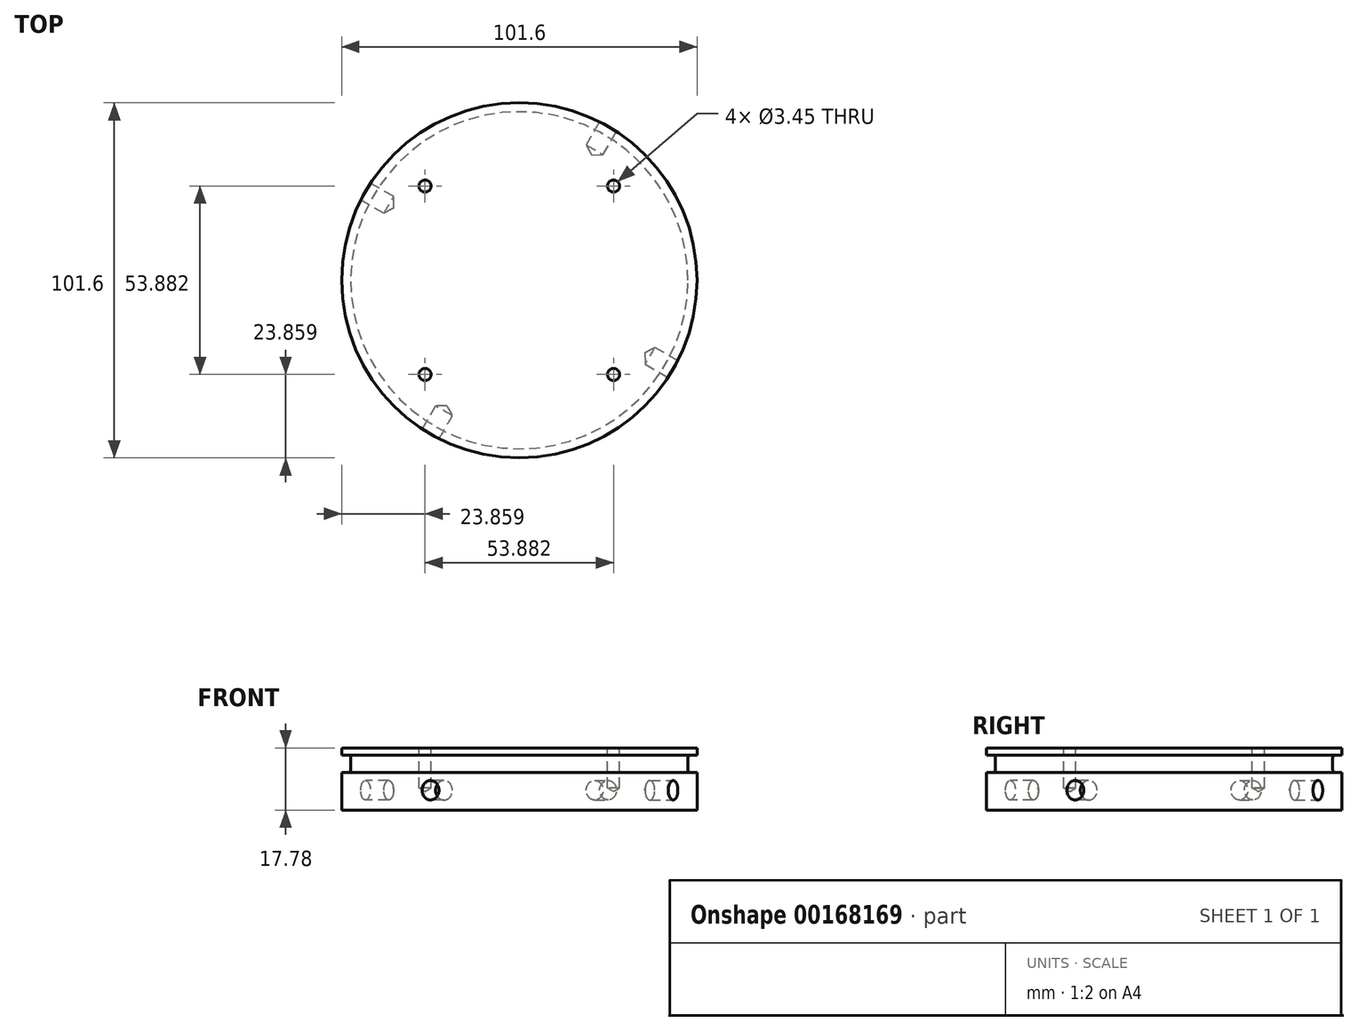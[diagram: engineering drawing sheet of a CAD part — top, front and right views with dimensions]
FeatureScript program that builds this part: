
annotation { "Feature Type Name" : "Feature", "Feature Type Description" : "" }
export const myFeature = defineFeature(function(context is Context, id is Id, definition is map)
    precondition{}
    {
        {
            var Q0;
            Q0=qCreatedBy(makeId("Top.planeOp"),FACE);
            var sketch = newSketch(context, id + "F0", { "sketchPlane" : qUnion([Q0])});
            skCircle(sketch, "E0", {"center": v(0, 0) * mm, "radius": 50.8 * mm});
            skSolve(sketch);
        }
        {
            var Q0;
            Q0=makeQuery(id+"F0.imprint","IMPRINT",FACE,{"disambiguationData":[TD([[makeQuery(id+"F0.imprint","IMPRINT",EDGE,{"derivedFrom":sQuery(id+"F0.wireOp",EDGE,"E0")}),1.0]])]});
            extrude(context, id + "F1", {"entities" : qUnion([Q0]), "depth" : 17.78 * mm});
        }
        {
            var Q0;
            {var subQ0=makeQuery(id+"FhJubWmbG7UBd7M_1.boolean.opBoolean","COPY",FACE,{"derivedFrom":makeQuery(id+"FhJubWmbG7UBd7M_1.opExtrude","SWEPT_FACE",FACE,{"disambiguationData":[OSD([sQuery(id+"FRuIeaWD6VeLny9_1.wireOp",EDGE,"idePJaX5-tPPE-BKw2-N1m4-zZUQrY6AHjir")])]})});Q0=makeQuery(id+"FOQC5dfjhO448EJ_1.boolean.opBoolean","SPLIT",FACE,{"disambiguationData":[TD([subQ0])],"derivedFrom":makeQuery(id+"FkcieFRIapZdHPD_1.boolean.opBoolean","SPLIT",FACE,{"disambiguationData":[TD([subQ0])],"derivedFrom":makeQuery(id+"F1.opExtrude","CAP_FACE",FACE,{"disambiguationData":[OSD([sQuery(id+"F0.wireOp",EDGE,"E0")])],"isStart":false})})});}
            var sketch = newSketch(context, id + "F2", { "sketchPlane" : qUnion([Q0])});
            skCircle(sketch, "E1", {"center": v(0, 0) * mm, "radius": 38.1 * mm, "construction": true});
            skLineSegment(sketch, "E2", {"start": v(0, 0) * mm, "end": v(38.1, 0) * mm, "construction": true});
            skPoint(sketch, "E3", {"position": v(38.1, 0) * mm});
            skLineSegment(sketch, "E4", {"start": v(0, 0) * mm, "end": v(26.94, -26.94) * mm, "construction": true});
            skPoint(sketch, "E5", {"position": v(26.94, -26.94) * mm});
            skPoint(sketch, "E6.1.0", {"position": v(26.94, 26.94) * mm});
            skPoint(sketch, "E6.2.0", {"position": v(-26.94, 26.94) * mm});
            skPoint(sketch, "E6.3.0", {"position": v(-26.94, -26.94) * mm});
            skSolve(sketch);
        }
        {
            var Q0;
            Q0=sQuery(id+"F2.wireOp",VERTEX,"E5");
            var Q1;
            Q1=sQuery(id+"F2.wireOp",VERTEX,"E6.3.0");
            var Q2;
            Q2=sQuery(id+"F2.wireOp",VERTEX,"E6.2.0");
            var Q3;
            Q3=sQuery(id+"F2.wireOp",VERTEX,"E6.1.0");
            var Q4;
            Q4=makeQuery(id+"F1.opExtrude","SWEPT_BODY",BODY,{"disambiguationData":[OSD([sQuery(id+"F0.wireOp",EDGE,"E0")])]});
            hole(context, id + "F3", {"style" : HoleStyle.SIMPLE, "endStyle" : HoleEndStyle.BLIND, "standardTappedOrClearance" : lookupTablePath({ "standard" : "ANSI", "engagement" : "75%", "pitch" : "32 tpi", "size" : "#8", "type" : "Tapped" }), "standardBlindInLast" : lookupTablePath({ "standard" : "ANSI", "engagement" : "75%", "pitch" : "32 tpi", "size" : "#8", "type" : "Tapped" }), "holeDiameter" : 3.45 * mm, "holeDepth" : 11.43 * mm, "locations" : qUnion([Q0, Q1, Q2, Q3]), "scope" : qUnion([Q4]), "majorDiameter" : 4.17 * mm});
        }
        {
            var Q0;
            Q0=makeQuery(id+"FOQC5dfjhO448EJ_1.boolean.opBoolean","SPLIT",FACE,{"disambiguationData":[TD([makeQuery(id+"FhJubWmbG7UBd7M_1.boolean.opBoolean","COPY",FACE,{"derivedFrom":makeQuery(id+"FhJubWmbG7UBd7M_1.opExtrude","SWEPT_FACE",FACE,{"disambiguationData":[OSD([sQuery(id+"FRuIeaWD6VeLny9_1.wireOp",EDGE,"idePJaX5-tPPE-BKw2-N1m4-zZUQrY6AHjir")])]})})])],"derivedFrom":makeQuery(id+"F1.opExtrude","CAP_FACE",FACE,{"disambiguationData":[OSD([sQuery(id+"F0.wireOp",EDGE,"E0")])],"isStart":false})});
            cPlane(context, id + "F4", {"entities" : qUnion([Q0]), "cplaneType" : CPlaneType.OFFSET, "offset" : 2.03 * mm, "oppositeDirection" : true, "width" : 152.4 * mm, "height" : 152.4 * mm});
        }
        {
            var Q0;
            Q0=qCreatedBy(id+"F4.planeOp",FACE);
            var sketch = newSketch(context, id + "F5", { "sketchPlane" : qUnion([Q0])});
            skCircle(sketch, "E7", {"center": v(0, 0) * mm, "radius": 48.2 * mm});
            skCircle(sketch, "E8.0", {"center": v(0, 0) * mm, "radius": 50.8 * mm});
            skSolve(sketch);
        }
        {
            var Q0;
            Q0=qSketchRegion(id+"F5",true);
            extrude(context, id + "F6", {"entities" : qUnion([Q0]), "operationType" : NewBodyOperationType.REMOVE, "oppositeDirection" : true, "depth" : 5 * mm});
        }
        {
            var Q0;
            Q0=makeQuery(id+"F6.boolean.opBoolean","COPY",EDGE,{"derivedFrom":makeQuery(id+"F6.opExtrude","CAP_EDGE",EDGE,{"disambiguationData":[OSD([sQuery(id+"F5.wireOp",EDGE,"E7")])],"isStart":false})});
            var Q1;
            Q1=makeQuery(id+"F6.boolean.opBoolean","COPY",EDGE,{"derivedFrom":makeQuery(id+"F6.opExtrude","CAP_EDGE",EDGE,{"disambiguationData":[OSD([sQuery(id+"F5.wireOp",EDGE,"E7")])],"isStart":true})});
            fillet(context, id + "F7", {"entities" : qUnion([Q0, Q1]), "radius" : 0.76 * mm, "tangentPropagation" : true, "allowEdgeOverflow" : false});
        }
        {
            var Q0;
            {var subQ1=sQuery(id+"F0.wireOp",EDGE,"E0");var subQ2=makeQuery(id+"F1.opExtrude","SWEPT_FACE",FACE,{"disambiguationData":[OSD([subQ1])]});Q0=makeQuery(id+"FkcieFRIapZdHPD_1.boolean.opBoolean","SPLIT",FACE,{"disambiguationData":[TD([subQ2])],"derivedFrom":makeQuery(id+"F1.opExtrude","CAP_FACE",FACE,{"disambiguationData":[OSD([subQ1])],"isStart":false})});}
            var sketch = newSketch(context, id + "F8", { "sketchPlane" : qUnion([Q0])});
            skCircle(sketch, "E9.0", {"center": v(0, 0) * mm, "radius": 50.8 * mm, "construction": true});
            skPoint(sketch, "E10", {"position": v(-25.4, -44) * mm});
            skLineSegment(sketch, "E11", {"start": v(0, -50.8) * mm, "end": v(0, 0) * mm, "construction": true});
            skLineSegment(sketch, "E12", {"start": v(0, 0) * mm, "end": v(-17.96, -31.1) * mm, "construction": true});
            skLineSegment(sketch, "E13", {"start": v(-17.96, -31.1) * mm, "end": v(-25.4, -44) * mm, "construction": true});
            skLineSegment(sketch, "E14", {"start": v(0, 0) * mm, "end": v(25.4, 44) * mm, "construction": true});
            skLineSegment(sketch, "E15", {"start": v(25.4, 44) * mm, "end": v(0, 0) * mm, "construction": true});
            skLineSegment(sketch, "E16", {"start": v(44, -25.4) * mm, "end": v(0, 0) * mm, "construction": true});
            skLineSegment(sketch, "E17", {"start": v(0, 0) * mm, "end": v(-44, 25.4) * mm, "construction": true});
            skPoint(sketch, "E18", {"position": v(25.4, 44) * mm});
            skPoint(sketch, "E19", {"position": v(44, -25.4) * mm});
            skPoint(sketch, "E20", {"position": v(-44, 25.4) * mm});
            skSolve(sketch);
        }
        {
            var Q0;
            Q0=qCreatedBy(makeId("Front.planeOp"),FACE);
            var sketch = newSketch(context, id + "F9", { "sketchPlane" : qUnion([Q0])});
            skLineSegment(sketch, "E21", {"start": v(0, 0) * mm, "end": v(0, 38.57) * mm, "construction": true});
            skSolve(sketch);
        }
        {
            var Q0;
            Q0=sQuery(id+"F9.wireOp",EDGE,"E21");
            cPlane(context, id + "F10", {"entities" : qUnion([Q0]), "cplaneType" : CPlaneType.LINE_ANGLE, "offset" : 25.4 * mm, "angle" : 60 * degree, "width" : 152.4 * mm, "height" : 152.4 * mm});
        }
        {
            var Q0;
            Q0=sQuery(id+"F8.wireOp",VERTEX,"E10");
            var Q1;
            Q1=qCreatedBy(id+"F10.planeOp",FACE);
            cPlane(context, id + "F11", {"entities" : qUnion([Q0, Q1]), "cplaneType" : CPlaneType.PLANE_POINT, "offset" : 25.4 * mm, "width" : 152.4 * mm, "height" : 152.4 * mm});
        }
        {
            var Q0;
            Q0=qCreatedBy(id+"F11.planeOp",FACE);
            var Q1;
            Q1=sQuery(id+"F8.wireOp",VERTEX,"E18");
            cPlane(context, id + "F12", {"entities" : qUnion([Q0, Q1]), "cplaneType" : CPlaneType.PLANE_POINT, "offset" : 25.4 * mm, "width" : 152.4 * mm, "height" : 152.4 * mm});
        }
        {
            var Q0;
            Q0=sQuery(id+"F9.wireOp",EDGE,"E21");
            cPlane(context, id + "F13", {"entities" : qUnion([Q0]), "cplaneType" : CPlaneType.LINE_ANGLE, "offset" : 25.4 * mm, "angle" : 150 * degree, "width" : 152.4 * mm, "height" : 152.4 * mm});
        }
        {
            var Q0;
            Q0=sQuery(id+"F8.wireOp",VERTEX,"E20");
            var Q1;
            Q1=qCreatedBy(id+"F13.planeOp",FACE);
            cPlane(context, id + "F14", {"entities" : qUnion([Q0, Q1]), "cplaneType" : CPlaneType.PLANE_POINT, "offset" : 25.4 * mm, "width" : 152.4 * mm, "height" : 152.4 * mm});
        }
        {
            var Q0;
            Q0=qCreatedBy(id+"F13.planeOp",FACE);
            var Q1;
            Q1=sQuery(id+"F8.wireOp",VERTEX,"E19");
            cPlane(context, id + "F15", {"entities" : qUnion([Q0, Q1]), "cplaneType" : CPlaneType.PLANE_POINT, "offset" : 25.4 * mm, "width" : 152.4 * mm, "height" : 152.4 * mm});
        }
        {
            var Q0;
            Q0=qCreatedBy(id+"F11.planeOp",FACE);
            var sketch = newSketch(context, id + "F16", { "sketchPlane" : qUnion([Q0])});
            skLineSegment(sketch, "E22", {"start": v(0, 0) * mm, "end": v(0, 5.66) * mm, "construction": true});
            skPoint(sketch, "E23", {"position": v(0, 5.66) * mm});
            skSolve(sketch);
        }
        {
            var Q0;
            Q0=qCreatedBy(id+"F12.planeOp",FACE);
            var sketch = newSketch(context, id + "F17", { "sketchPlane" : qUnion([Q0])});
            skPoint(sketch, "E24", {"position": v(0, 5.66) * mm});
            skLineSegment(sketch, "E25.0", {"start": v(0, 0) * mm, "end": v(0, 5.66) * mm, "construction": true});
            skSolve(sketch);
        }
        {
            var Q0;
            Q0=qCreatedBy(id+"F14.planeOp",FACE);
            var sketch = newSketch(context, id + "F18", { "sketchPlane" : qUnion([Q0])});
            skLineSegment(sketch, "E26", {"start": v(0, 0) * mm, "end": v(0, 5.66) * mm, "construction": true});
            skLineSegment(sketch, "E27.0", {"start": v(-50.8, 0) * mm, "end": v(-50.8, 5.66) * mm, "construction": true});
            skPoint(sketch, "E28", {"position": v(0, 5.66) * mm});
            skLineSegment(sketch, "E29", {"start": v(-50.8, 5.66) * mm, "end": v(0, 5.66) * mm, "construction": true});
            skSolve(sketch);
        }
        {
            var Q0;
            Q0=qCreatedBy(id+"F15.planeOp",FACE);
            var sketch = newSketch(context, id + "F19", { "sketchPlane" : qUnion([Q0])});
            skLineSegment(sketch, "E30.0", {"start": v(0, 0) * mm, "end": v(0, 5.66) * mm, "construction": true});
            skPoint(sketch, "E31", {"position": v(0, 5.66) * mm});
            skSolve(sketch);
        }
        {
            var Q0;
            Q0=sQuery(id+"F19.wireOp",VERTEX,"E31");
            var Q1;
            Q1=makeQuery(id+"F1.opExtrude","SWEPT_BODY",BODY,{"disambiguationData":[OSD([sQuery(id+"F0.wireOp",EDGE,"E0")])]});
            hole(context, id + "F20", {"style" : HoleStyle.SIMPLE, "endStyle" : HoleEndStyle.BLIND, "oppositeDirection" : true, "standardTappedOrClearance" : lookupTablePath({ "standard" : "ANSI", "engagement" : "75%", "pitch" : "32 tpi", "size" : "1/4", "type" : "Tapped" }), "standardBlindInLast" : lookupTablePath({ "standard" : "ANSI", "engagement" : "75%", "pitch" : "32 tpi", "size" : "1/4", "type" : "Tapped" }), "holeDiameter" : 5.56 * mm, "holeDepth" : 7.62 * mm, "locations" : qUnion([Q0]), "scope" : qUnion([Q1]), "majorDiameter" : 6.35 * mm});
        }
        {
            var Q0;
            Q0=sQuery(id+"F18.wireOp",VERTEX,"E28");
            var Q1;
            Q1=makeQuery(id+"F1.opExtrude","SWEPT_BODY",BODY,{"disambiguationData":[OSD([sQuery(id+"F0.wireOp",EDGE,"E0")])]});
            hole(context, id + "F21", {"style" : HoleStyle.SIMPLE, "endStyle" : HoleEndStyle.BLIND, "standardTappedOrClearance" : lookupTablePath({ "standard" : "ANSI", "engagement" : "75%", "pitch" : "32 tpi", "size" : "1/4", "type" : "Tapped" }), "standardBlindInLast" : lookupTablePath({ "standard" : "ANSI", "engagement" : "75%", "pitch" : "32 tpi", "size" : "1/4", "type" : "Tapped" }), "holeDiameter" : 5.56 * mm, "holeDepth" : 7.62 * mm, "locations" : qUnion([Q0]), "scope" : qUnion([Q1]), "majorDiameter" : 6.35 * mm});
        }
        {
            var Q0;
            Q0=sQuery(id+"F16.wireOp",VERTEX,"E23");
            var Q1;
            Q1=makeQuery(id+"F1.opExtrude","SWEPT_BODY",BODY,{"disambiguationData":[OSD([sQuery(id+"F0.wireOp",EDGE,"E0")])]});
            hole(context, id + "F22", {"style" : HoleStyle.SIMPLE, "endStyle" : HoleEndStyle.BLIND, "oppositeDirection" : true, "standardTappedOrClearance" : lookupTablePath({ "standard" : "ANSI", "engagement" : "75%", "pitch" : "32 tpi", "size" : "1/4", "type" : "Tapped" }), "standardBlindInLast" : lookupTablePath({ "standard" : "ANSI", "engagement" : "75%", "pitch" : "32 tpi", "size" : "1/4", "type" : "Tapped" }), "holeDiameter" : 5.56 * mm, "holeDepth" : 7.62 * mm, "locations" : qUnion([Q0]), "scope" : qUnion([Q1]), "majorDiameter" : 6.35 * mm});
        }
        {
            var Q0;
            Q0=sQuery(id+"F17.wireOp",VERTEX,"E24");
            var Q1;
            Q1=makeQuery(id+"F1.opExtrude","SWEPT_BODY",BODY,{"disambiguationData":[OSD([sQuery(id+"F0.wireOp",EDGE,"E0")])]});
            hole(context, id + "F23", {"style" : HoleStyle.SIMPLE, "endStyle" : HoleEndStyle.BLIND, "standardTappedOrClearance" : lookupTablePath({ "standard" : "ANSI", "engagement" : "75%", "pitch" : "32 tpi", "size" : "1/4", "type" : "Tapped" }), "standardBlindInLast" : lookupTablePath({ "standard" : "ANSI", "engagement" : "75%", "pitch" : "32 tpi", "size" : "1/4", "type" : "Tapped" }), "holeDiameter" : 5.56 * mm, "holeDepth" : 7.62 * mm, "locations" : qUnion([Q0]), "scope" : qUnion([Q1]), "majorDiameter" : 6.35 * mm});
        }
    });
